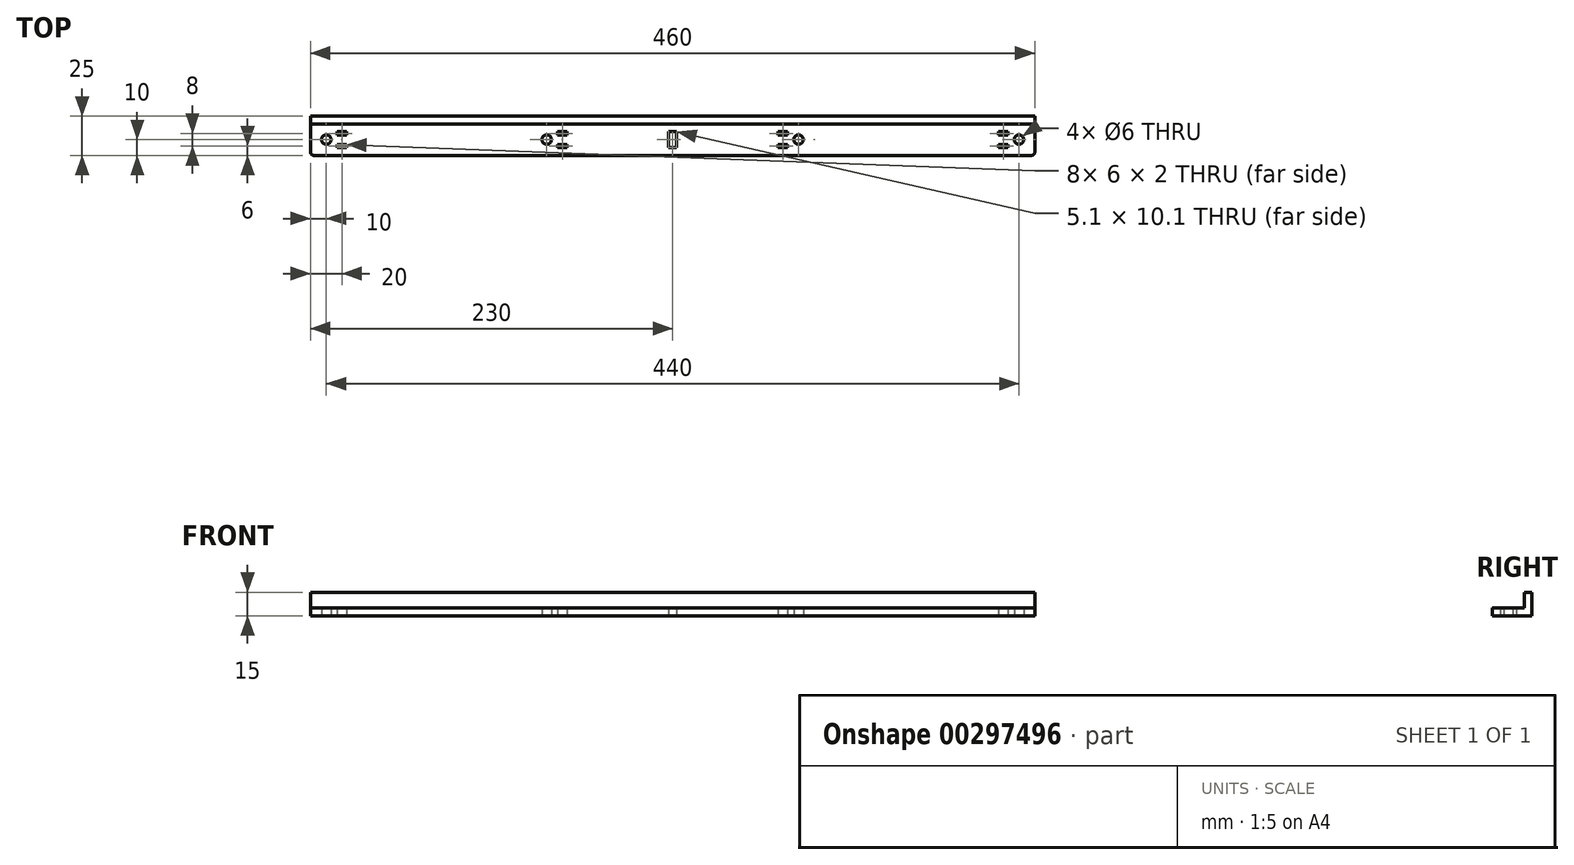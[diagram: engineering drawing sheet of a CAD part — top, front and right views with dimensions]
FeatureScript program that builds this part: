
annotation { "Feature Type Name" : "Feature", "Feature Type Description" : "" }
export const myFeature = defineFeature(function(context is Context, id is Id, definition is map)
    precondition{}
    {
        {
            var Q0;
            Q0=qCreatedBy(makeId("Top.planeOp"),FACE);
            var sketch = newSketch(context, id + "F0", { "sketchPlane" : qUnion([Q0])});
            skCircle(sketch, "E0", {"center": v(-70, 0) * mm, "radius": 3 * mm});
            skCircle(sketch, "E1.MirrorC", {"center": v(70, 0) * mm, "radius": 3 * mm});
            skCircle(sketch, "E2", {"center": v(230, 0) * mm, "radius": 3 * mm});
            skCircle(sketch, "E3.MirrorC", {"center": v(370, 0) * mm, "radius": 3 * mm});
            skPoint(sketch, "E4", {"position": v(150, 0) * mm});
            skLineSegment(sketch, "E5.bottom", {"start": v(-78, -10) * mm, "end": v(378, -10) * mm});
            skLineSegment(sketch, "E5.top", {"start": v(-80, 15) * mm, "end": v(380, 15) * mm});
            skLineSegment(sketch, "E5.left", {"start": v(-80, -8) * mm, "end": v(-80, 15) * mm});
            skLineSegment(sketch, "E5.right", {"start": v(380, -8) * mm, "end": v(380, 15) * mm});
            skPoint(sketch, "E5.middle", {"position": v(150, 3) * mm});
            skLineSegment(sketch, "E6.bottom", {"start": v(152.55, -5.05) * mm, "end": v(147.45, -5.05) * mm});
            skLineSegment(sketch, "E6.top", {"start": v(152.55, 5.05) * mm, "end": v(147.45, 5.05) * mm});
            skLineSegment(sketch, "E6.left", {"start": v(152.55, -5.05) * mm, "end": v(152.55, 5.05) * mm});
            skLineSegment(sketch, "E6.right", {"start": v(147.45, -5.05) * mm, "end": v(147.45, 5.05) * mm});
            skPoint(sketch, "E7.visualSharp", {"position": v(-80, -10) * mm});
            skArc(sketch, "E7.filletArc", {"start": v(-80, -8) * mm, "mid": v(-79.41, -9.41) * mm, "end": v(-78, -10) * mm});
            skPoint(sketch, "E8.visualSharp", {"position": v(380, -10) * mm});
            skArc(sketch, "E8.filletArc", {"start": v(378, -10) * mm, "mid": v(379.41, -9.41) * mm, "end": v(380, -8) * mm});
            skLineSegment(sketch, "E9.bottom", {"start": v(-63, 5) * mm, "end": v(-57, 5) * mm});
            skLineSegment(sketch, "E9.top", {"start": v(-63, 3) * mm, "end": v(-57, 3) * mm});
            skLineSegment(sketch, "E9.left", {"start": v(-63, 5) * mm, "end": v(-63, 3) * mm});
            skLineSegment(sketch, "E9.right", {"start": v(-57, 5) * mm, "end": v(-57, 3) * mm});
            skLineSegment(sketch, "E10.bottom", {"start": v(-63, -3) * mm, "end": v(-57, -3) * mm});
            skLineSegment(sketch, "E10.top", {"start": v(-63, -5) * mm, "end": v(-57, -5) * mm});
            skLineSegment(sketch, "E10.left", {"start": v(-63, -3) * mm, "end": v(-63, -5) * mm});
            skLineSegment(sketch, "E10.right", {"start": v(-57, -3) * mm, "end": v(-57, -5) * mm});
            skPoint(sketch, "E11", {"position": v(-50, 0) * mm});
            skLineSegment(sketch, "E12.bottom", {"start": v(77, 5) * mm, "end": v(83, 5) * mm});
            skLineSegment(sketch, "E12.top", {"start": v(77, 3) * mm, "end": v(83, 3) * mm});
            skLineSegment(sketch, "E12.left", {"start": v(77, 5) * mm, "end": v(77, 3) * mm});
            skLineSegment(sketch, "E12.right", {"start": v(83, 5) * mm, "end": v(83, 3) * mm});
            skLineSegment(sketch, "E13.bottom", {"start": v(77, -3) * mm, "end": v(83, -3) * mm});
            skLineSegment(sketch, "E13.top", {"start": v(77, -5) * mm, "end": v(83, -5) * mm});
            skLineSegment(sketch, "E13.left", {"start": v(77, -3) * mm, "end": v(77, -5) * mm});
            skLineSegment(sketch, "E13.right", {"start": v(83, -3) * mm, "end": v(83, -5) * mm});
            skPoint(sketch, "E14", {"position": v(90, 0) * mm});
            skPoint(sketch, "E15", {"position": v(210, 0) * mm});
            skLineSegment(sketch, "E16.bottom", {"start": v(217, 5) * mm, "end": v(223, 5) * mm});
            skLineSegment(sketch, "E16.top", {"start": v(217, 3) * mm, "end": v(223, 3) * mm});
            skLineSegment(sketch, "E16.left", {"start": v(217, 5) * mm, "end": v(217, 3) * mm});
            skLineSegment(sketch, "E16.right", {"start": v(223, 5) * mm, "end": v(223, 3) * mm});
            skLineSegment(sketch, "E17.bottom", {"start": v(217, -3) * mm, "end": v(223, -3) * mm});
            skLineSegment(sketch, "E17.top", {"start": v(217, -5) * mm, "end": v(223, -5) * mm});
            skLineSegment(sketch, "E17.left", {"start": v(217, -3) * mm, "end": v(217, -5) * mm});
            skLineSegment(sketch, "E17.right", {"start": v(223, -3) * mm, "end": v(223, -5) * mm});
            skPoint(sketch, "E18", {"position": v(350, 0) * mm});
            skLineSegment(sketch, "E19.bottom", {"start": v(357, 5) * mm, "end": v(363, 5) * mm});
            skLineSegment(sketch, "E19.top", {"start": v(357, 3) * mm, "end": v(363, 3) * mm});
            skLineSegment(sketch, "E19.left", {"start": v(357, 5) * mm, "end": v(357, 3) * mm});
            skLineSegment(sketch, "E19.right", {"start": v(363, 5) * mm, "end": v(363, 3) * mm});
            skLineSegment(sketch, "E20.bottom", {"start": v(357, -3) * mm, "end": v(363, -3) * mm});
            skLineSegment(sketch, "E20.top", {"start": v(357, -5) * mm, "end": v(363, -5) * mm});
            skLineSegment(sketch, "E20.left", {"start": v(357, -3) * mm, "end": v(357, -5) * mm});
            skLineSegment(sketch, "E20.right", {"start": v(363, -3) * mm, "end": v(363, -5) * mm});
            skLineSegment(sketch, "E21.top", {"start": v(-80, 10) * mm, "end": v(380, 10) * mm});
            skLineSegment(sketch, "E21.left", {"start": v(-80, 15) * mm, "end": v(-80, 10) * mm});
            skLineSegment(sketch, "E21.right", {"start": v(380, 15) * mm, "end": v(380, 10) * mm});
            skSolve(sketch);
        }
        {
            var Q0;
            Q0=makeQuery(id+"F0.imprint","IMPRINT",FACE,{"disambiguationData":[TD([[makeQuery(id+"F0.imprint","IMPRINT",EDGE,{"derivedFrom":sQuery(id+"F0.wireOp",EDGE,"E0")}),-1.0]])]});
            extrude(context, id + "F1", {"entities" : qUnion([Q0]), "depth" : 5 * mm});
        }
        {
            var Q0;
            Q0=makeQuery(id+"F0.imprint","IMPRINT",FACE,{"disambiguationData":[TD([[makeQuery(id+"F0.imprint","IMPRINT",EDGE,{"derivedFrom":sQuery(id+"F0.wireOp",EDGE,"E5.top")}),-1.0]])]});
            extrude(context, id + "F2", {"entities" : qUnion([Q0]), "operationType" : NewBodyOperationType.ADD, "depth" : 15 * mm});
        }
    });
